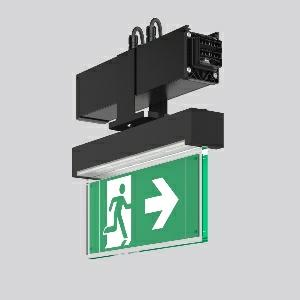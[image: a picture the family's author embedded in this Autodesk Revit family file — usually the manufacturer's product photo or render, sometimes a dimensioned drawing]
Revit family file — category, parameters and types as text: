
# Revit family: linedo_module_rz_9503rz_763_437_023_b9d3
name_source: partatom
category: Lighting Fixtures
units: mm (PartAtom-declared; Revit-internal decimal feet)

## family parameters
Cut with Voids When Loaded = No
Host = Face
Light Source = No
Part Type = Normal
Room Calculation Point = No
Round Connector Dimension = Use Diameter
Shared = No

## types (1)
- LINEDO Module RZ
    Apparent Load = 0 VA
    Default Elevation = 1800 mm
    Description = LINEDO, black, on/off
Continuous line luminaire, L 336 B 62 H 308, SBS, 3 h, DALI-Sibe
    Height = 308 mm
    Lamp = 0 x
    Length = 336 mm
    Luminous efficacy = 0 lm/W
    Manufacturer = RZB
    ModVariant = No
    Model = 9503RZ.763.437.023
    Mounting Place = Ceiling
    Mounting Type = Surface mounted
    Number of Poles = 1
    OnlyDefault = Yes
    Power Factor = 1
    Product Name = LINEDO Module RZ
    Product group = Continuous line luminaire system Linedo IP 54
    ProductGroupID = 314
    Protection Class = Protection class I
    Protection Degree = IP 54
    RLX_Detail_Level = 1
    RLX_Emergency_Light_Flux = 0 lm
    RLX_Emergency_Type = 0
    RLX_Emergency_Type_DB = No
    RlxData = <blob elided: 37373 chars, md5=9e7f8cae>
    Standby Power = 0 W
    System Light Flux = 0 lm
    System Power = 0 W
    Type Comments = Product without accessories
    Type Image = 9503rz.763.434.023.jpg
    URL = http://relux.com
    VarID = ---
    Voltage = 0 V
    Weight = 0.00 kg
    Width = 62 mm  [stored 0.203412 ft]

note: [stored X ft] marks values corroborated as IEEE doubles in the binary element streams (Revit-internal decimal feet)

## geometry (parser evidence)
native form markers: Blend x4, Sweep x11
no freeform markers — native parametric forms only
